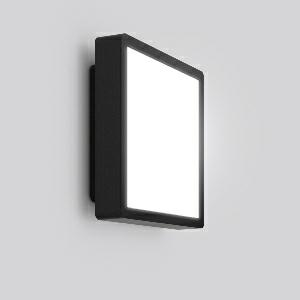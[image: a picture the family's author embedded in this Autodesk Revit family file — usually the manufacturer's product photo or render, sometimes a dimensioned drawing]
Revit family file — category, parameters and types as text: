
# Revit family: hb_107_612140_0031_def0
name_source: partatom
category: Lighting Fixtures
units: mm (PartAtom-declared; Revit-internal decimal feet)

## family parameters
Cut with Voids When Loaded = No
Host = Face
Light Source = No
Part Type = Normal
Room Calculation Point = No
Round Connector Dimension = Use Diameter
Shared = No

## types (1)
- HB 107 (1 x LED Modul 830, 1100 lm, 3000)
    Apparent Load = 15 VA
    CIE Flux Codes = 48 80 96 100 100
    Color Rendering = 80
    Color Temperature = 3000
    Default Elevation = 1800 mm
    Description = Series: HB 107
Wall luminaire. Housing: die-cast aluminium, powder-coated. Diffuser: plastic (polycarbonate), opal. Driver integrated. 
Colour: anthracite metallic (DB703)
Length: 236 mm
Width: 236 mm
Height: 68 mm
Lamp: LED
System power: 15 W
Rated luminous flux: 1100 lm
Luminous efficiency: 73 lm/W
Control gear: Converter not necessary
Protection class: I
Type of protection: IP 54
    Height = 68 mm
    Lamp = 1 x LED Modul 830
    Lamp Light Flux = 1100 lm
    Lamp count = 1
    Length = 236 mm
    Lifetime = 50000 h
    Luminous efficacy = 73 lm/W
    Manufacturer = RZB
    ModVariant = No
    Model = 612140.0031
    Mounting Place = Wall
    Mounting Type = Surface mounted
    Number of Poles = 1
    OnlyDefault = Yes
    Power Factor = 1
    Product Name = HB 107
    Product group = Surface mounted Wall luminaires
    ProductGroupID = 2001
    Protection Class = Protection class I
    Protection Degree = IP 54
    RLX_Detail_Level = 1
    RLX_Emergency_Light_Flux = 0 lm
    RLX_Emergency_Type = 0
    RLX_Emergency_Type_DB = No
    RlxData = <blob elided: 27241 chars, md5=55633bfb>
    Socket = socket
    Standby Power = 0 W
    System Light Flux = 1100 lm
    System Power = 15 W
    Type Comments = Product without accessories
    Type Image = 612140.0031.jpg
    URL = http://relux.com
    VarID = ---
    Voltage = 230 V
    Voltage Range = 220-240 V
    Weight = 0.00 kg
    Width = 236 mm

## geometry (parser evidence)
native form markers: Blend x4, Sweep x12
no freeform markers — native parametric forms only
